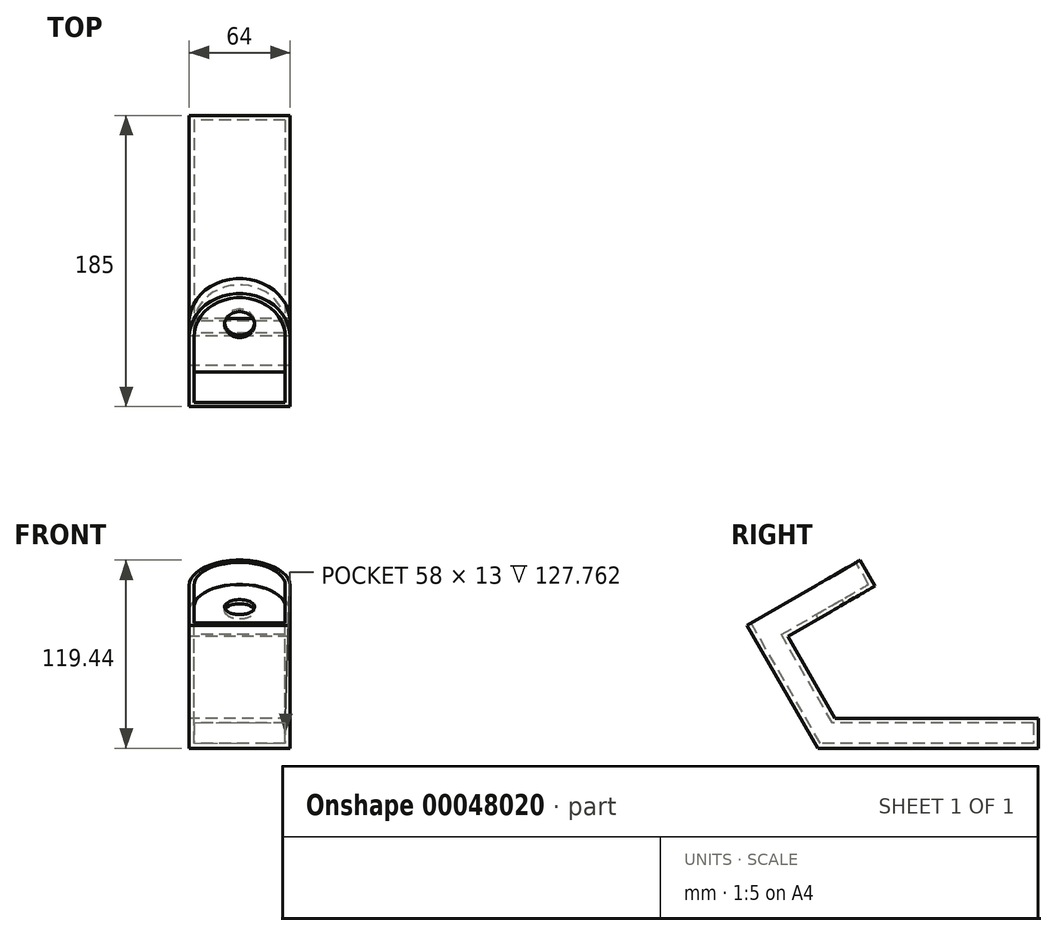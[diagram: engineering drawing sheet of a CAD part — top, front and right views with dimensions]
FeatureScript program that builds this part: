
annotation { "Feature Type Name" : "Feature", "Feature Type Description" : "" }
export const myFeature = defineFeature(function(context is Context, id is Id, definition is map)
    precondition{}
    {
        {
            var Q0;
            Q0=qCreatedBy(makeId("Right.planeOp"),FACE);
            var sketch = newSketch(context, id + "F0", { "sketchPlane" : qUnion([Q0])});
            skLineSegment(sketch, "E0", {"start": v(140, 0) * mm, "end": v(0, 0) * mm});
            skLineSegment(sketch, "E1", {"start": v(0, 0) * mm, "end": v(-45, 77.94) * mm});
            skLineSegment(sketch, "E2", {"start": v(-45, 77.94) * mm, "end": v(26.88, 119.44) * mm});
            skLineSegment(sketch, "E3.0", {"start": v(-19.05, 70.99) * mm, "end": v(36.38, 102.99) * mm});
            skLineSegment(sketch, "E3.1", {"start": v(10.97, 19) * mm, "end": v(-19.05, 70.99) * mm});
            skLineSegment(sketch, "E3.2", {"start": v(140, 19) * mm, "end": v(10.97, 19) * mm});
            skLineSegment(sketch, "E4", {"start": v(26.88, 119.44) * mm, "end": v(36.38, 102.99) * mm});
            skLineSegment(sketch, "E5", {"start": v(140, 19) * mm, "end": v(140, 0) * mm});
            skSolve(sketch);
        }
        {
            var Q0;
            Q0 = qSketchRegion(id + "F0", true);
            extrude(context, id + "F1", {"entities" : qUnion([Q0]), "endBound" : BoundingType.SYMMETRIC, "depth" : 64 * mm});
        }
        {
            var Q0;
            Q0=makeQuery(id+"F1.opExtrude","CAP_EDGE",EDGE,{"disambiguationData":[OSD([sQuery(id+"F0.wireOp",EDGE,"E4")])],"isStart":true});
            var Q1;
            Q1=makeQuery(id+"F1.opExtrude","CAP_EDGE",EDGE,{"disambiguationData":[OSD([sQuery(id+"F0.wireOp",EDGE,"E4")])],"isStart":false});
            fillet(context, id + "F2", {"entities" : qUnion([Q0, Q1]), "radius" : 32 * mm, "tangentPropagation" : true, "allowEdgeOverflow" : false});
        }
        {
            var Q0;
            Q0=makeQuery(id+"F1.opExtrude","SWEPT_FACE",FACE,{"disambiguationData":[OSD([sQuery(id+"F0.wireOp",EDGE,"E2")])]});
            shell(context, id + "F3", {"entities" : qUnion([Q0]), "thickness" : 3 * mm});
        }
        {
            var Q0;
            Q0=makeQuery(id+"F3.opShell","OFFSET_FACE",FACE,{"disambiguationData":[OSD([sQuery(id+"F0.wireOp",EDGE,"E3.0")])]});
            var sketch = newSketch(context, id + "F4", { "sketchPlane" : qUnion([Q0])});
            skCircle(sketch, "E6", {"center": v(0, 51) * mm, "radius": 9.5 * mm});
            skSolve(sketch);
        }
        {
            var Q0;
            Q0 = qSketchRegion(id + "F4", true);
            extrude(context, id + "F5", {"entities" : qUnion([Q0]), "operationType" : NewBodyOperationType.REMOVE, "endBound" : BoundingType.UP_TO_NEXT, "oppositeDirection" : true, "depth" : 25 * mm});
        }
    });
